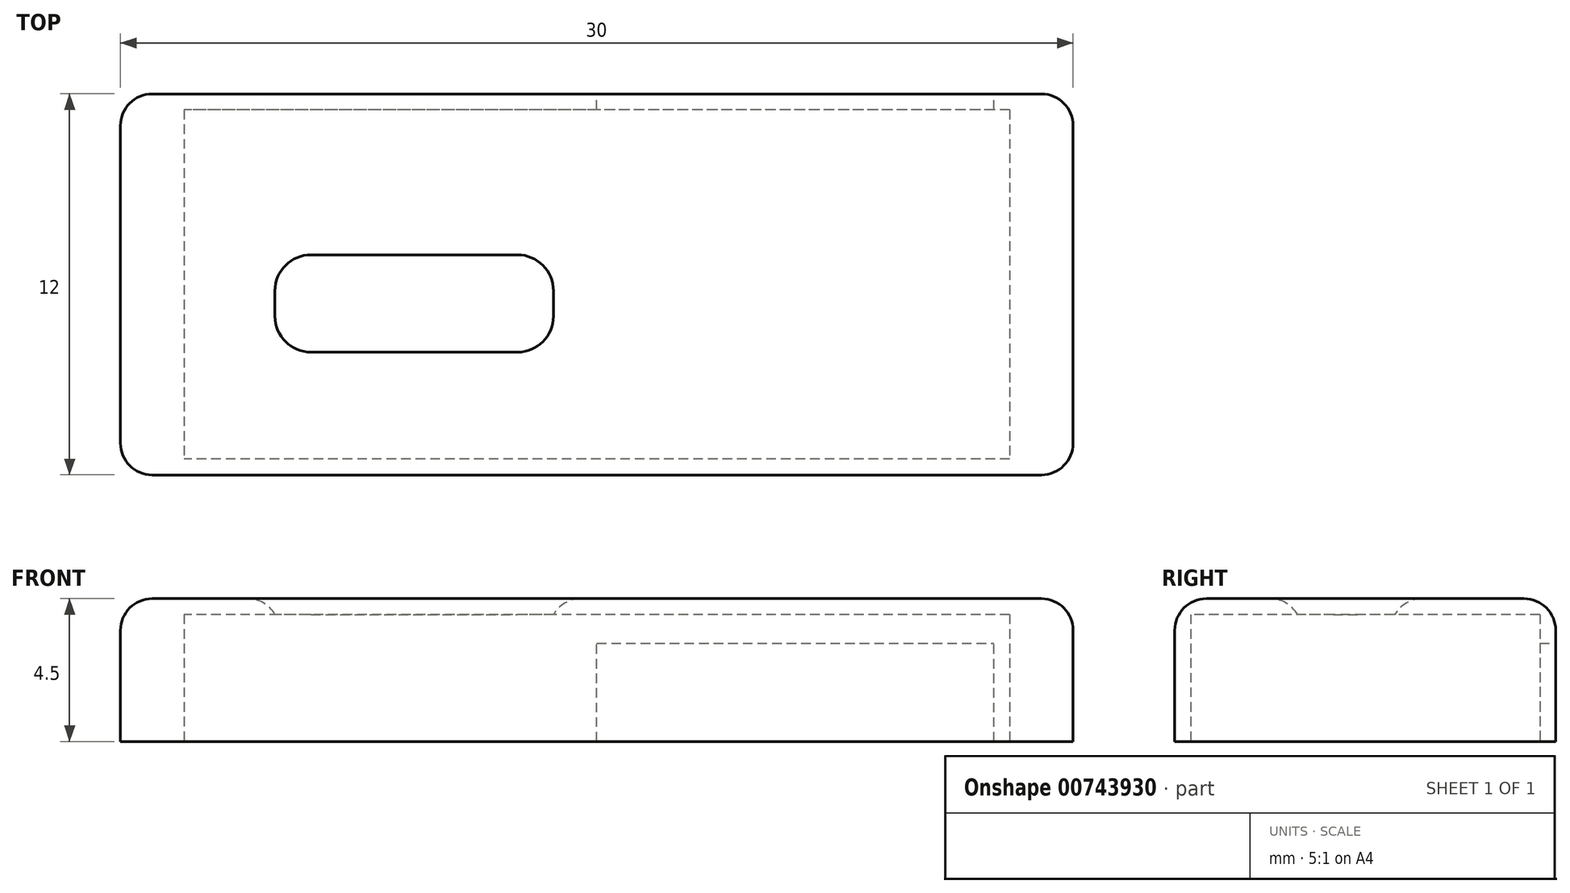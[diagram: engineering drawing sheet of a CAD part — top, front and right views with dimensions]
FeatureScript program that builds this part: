
annotation { "Feature Type Name" : "Feature", "Feature Type Description" : "" }
export const myFeature = defineFeature(function(context is Context, id is Id, definition is map)
    precondition{}
    {
        {
            var Q0;
            Q0=qCreatedBy(makeId("Top.planeOp"),FACE);
            var sketch = newSketch(context, id + "F0", { "sketchPlane" : qUnion([Q0])});
            skLineSegment(sketch, "E0.bottom", {"start": v(1, 2.88) * mm, "end": v(29, 2.88) * mm});
            skLineSegment(sketch, "E0.top", {"start": v(1, 14.88) * mm, "end": v(29, 14.88) * mm});
            skLineSegment(sketch, "E0.left", {"start": v(0, 3.88) * mm, "end": v(0, 13.88) * mm});
            skLineSegment(sketch, "E0.right", {"start": v(30, 3.88) * mm, "end": v(30, 13.88) * mm});
            skPoint(sketch, "E1.visualSharp", {"position": v(0, 14.88) * mm});
            skArc(sketch, "E1.filletArc", {"start": v(1, 14.88) * mm, "mid": v(0.3, 14.58) * mm, "end": v(0, 13.88) * mm});
            skPoint(sketch, "E2.visualSharp", {"position": v(30, 14.88) * mm});
            skArc(sketch, "E2.filletArc", {"start": v(30, 13.88) * mm, "mid": v(29.7, 14.58) * mm, "end": v(29, 14.88) * mm});
            skPoint(sketch, "E3.visualSharp", {"position": v(30, 2.88) * mm});
            skArc(sketch, "E3.filletArc", {"start": v(29, 2.88) * mm, "mid": v(29.7, 3.17) * mm, "end": v(30, 3.88) * mm});
            skPoint(sketch, "E4.visualSharp", {"position": v(0, 2.88) * mm});
            skArc(sketch, "E4.filletArc", {"start": v(0, 3.88) * mm, "mid": v(0.3, 3.17) * mm, "end": v(1, 2.88) * mm});
            skLineSegment(sketch, "E5.bottom", {"start": v(6, 9.68) * mm, "end": v(12.5, 9.68) * mm});
            skLineSegment(sketch, "E5.top", {"start": v(6, 6.88) * mm, "end": v(12.5, 6.88) * mm});
            skLineSegment(sketch, "E5.left", {"start": v(5, 8.68) * mm, "end": v(5, 7.88) * mm});
            skLineSegment(sketch, "E5.right", {"start": v(13.5, 8.68) * mm, "end": v(13.5, 7.88) * mm});
            skPoint(sketch, "E6.visualSharp", {"position": v(5, 9.68) * mm});
            skArc(sketch, "E6.filletArc", {"start": v(6, 9.68) * mm, "mid": v(5.3, 9.38) * mm, "end": v(5, 8.68) * mm});
            skPoint(sketch, "E7.visualSharp", {"position": v(5, 6.88) * mm});
            skArc(sketch, "E7.filletArc", {"start": v(5, 7.88) * mm, "mid": v(5.3, 7.17) * mm, "end": v(6, 6.88) * mm});
            skPoint(sketch, "E8.visualSharp", {"position": v(13.5, 9.68) * mm});
            skArc(sketch, "E8.filletArc", {"start": v(13.5, 8.68) * mm, "mid": v(13.2, 9.38) * mm, "end": v(12.5, 9.68) * mm});
            skPoint(sketch, "E9.visualSharp", {"position": v(13.5, 6.88) * mm});
            skArc(sketch, "E9.filletArc", {"start": v(12.5, 6.88) * mm, "mid": v(13.2, 7.17) * mm, "end": v(13.5, 7.88) * mm});
            skSolve(sketch);
        }
        {
            var Q0;
            Q0 = qSketchRegion(id + "F0", true);
            extrude(context, id + "F1", {"entities" : qUnion([Q0]), "depth" : 4.5 * mm, "offsetDistance" : 25 * mm});
        }
        {
            var Q0;
            Q0=makeQuery(id+"F1.opExtrude","CAP_FACE",FACE,{"disambiguationData":[OSD([sQuery(id+"F0.wireOp",EDGE,"E0.bottom"),sQuery(id+"F0.wireOp",EDGE,"E0.top"),sQuery(id+"F0.wireOp",EDGE,"E0.left"),sQuery(id+"F0.wireOp",EDGE,"E0.right")])],"isStart":false});
            fillet(context, id + "F2", {"entities" : qUnion([Q0]), "radius" : 1 * mm, "tangentPropagation" : true, "allowEdgeOverflow" : false});
        }
        {
            var Q0;
            Q0=qCreatedBy(makeId("Top.planeOp"),FACE);
            var sketch = newSketch(context, id + "F3", { "sketchPlane" : qUnion([Q0])});
            skLineSegment(sketch, "E10.bottom", {"start": v(28, 14.38) * mm, "end": v(2, 14.38) * mm});
            skLineSegment(sketch, "E10.top", {"start": v(28, 3.38) * mm, "end": v(2, 3.38) * mm});
            skLineSegment(sketch, "E10.left", {"start": v(28, 14.38) * mm, "end": v(28, 3.38) * mm});
            skLineSegment(sketch, "E10.right", {"start": v(2, 14.38) * mm, "end": v(2, 3.38) * mm});
            skLineSegment(sketch, "E11.bottom", {"start": v(14.5, 3.38) * mm, "end": v(27, 3.38) * mm});
            skSolve(sketch);
        }
        {
            var Q0;
            Q0 = qSketchRegion(id + "F3", true);
            extrude(context, id + "F4", {"entities" : qUnion([Q0]), "operationType" : NewBodyOperationType.REMOVE, "depth" : 4 * mm, "offsetDistance" : 25 * mm});
        }
        {
            var Q0;
            Q0=qCreatedBy(makeId("Top.planeOp"),FACE);
            var sketch = newSketch(context, id + "F5", { "sketchPlane" : qUnion([Q0])});
            skLineSegment(sketch, "E12.bottom", {"start": v(15, 13.29) * mm, "end": v(27.5, 13.29) * mm});
            skLineSegment(sketch, "E12.top", {"start": v(15, 16.27) * mm, "end": v(27.5, 16.27) * mm});
            skLineSegment(sketch, "E12.left", {"start": v(15, 13.29) * mm, "end": v(15, 16.27) * mm});
            skLineSegment(sketch, "E12.right", {"start": v(27.5, 13.29) * mm, "end": v(27.5, 16.27) * mm});
            skSolve(sketch);
        }
        {
            var Q0;
            Q0 = qSketchRegion(id + "F5", true);
            extrude(context, id + "F6", {"entities" : qUnion([Q0]), "operationType" : NewBodyOperationType.REMOVE, "depth" : 3.1 * mm, "offsetDistance" : 25 * mm});
        }
    });
